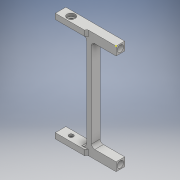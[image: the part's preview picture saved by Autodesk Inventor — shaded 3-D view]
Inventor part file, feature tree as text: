
AUTODESK INVENTOR PART (.ipt)
format: ipt  version: 2018 (Build 220112000, 112)  size: 381,952 bytes
history: native  units: mm
features: sketch x10, extrude x9, fillet x4
ambient origin geometry x8: Origin, YZ Plane, XZ Plane, XY Plane, X Axis, Y Axis, Z Axis, Center Point
bodies: Solid1 (feature_tree)
feature tree (23):
  extrude  "Extrusion1"  Depth=5.5118mm
  extrude  "Extrusion2"  Depth=2.3368mm
  extrude  "Extrusion3"  Depth=5.5118mm
  fillet  "Fillet1"  Radius=5.588mm
  fillet  "Fillet2"  Radius=2.3368mm
  extrude  "Extrusion4"  Depth=5.0mm
  extrude  "Extrusion5"  Depth=10.763mm
  extrude  "Extrusion6"  Depth=30.0mm TaperAngle=0.0deg
  extrude  "Extrusion7"  Depth=5.0mm
  fillet  "Fillet3"  Radius=10.763mm
  sketch  "Sketch8"  dims[d22=8.1mm d23=114.75mm d24=0.0mm]
  extrude  "Extrusion8"  Depth=114.75mm TaperAngle=0.0deg
  extrude  "Extrusion9"  Depth=2.412mm TaperAngle=0.0deg
  fillet  "Fillet4"  Radius=4.5mm
  sketch  "Sketch1"  dims[d0=8.763mm d1=5.5118mm]
  sketch  "Sketch2"  dims[d4=5.588mm d5=2.3368mm]
  sketch  "Sketch3"  dims[d6=8.763mm d7=5.5118mm d8=5.588mm d9=2.3368mm]
  sketch  "Sketch4"  dims[d10=30.0mm d11=0.0mm d12=5.0mm]
  sketch  "Sketch5"  dims[d13=111.0mm d14=0.0mm d15=10.763mm]
  sketch  "Sketch6"  dims[d16=10.763mm d17=30.0mm d18=0.0mm]
  sketch  "Sketch7"  dims[d19=2.0mm d20=5.0mm d21=10.763mm]
  sketch  "Sketch9"  dims[d25=2.412mm d26=0.0mm d27=2.412mm d28=0.0mm d29=4.5mm]
  sketch  "Sketch10"  dims[d30=115.0mm d31=0.0mm d32=0.5mm d33=8.763mm d34=8.763mm d35=29.5mm d36=0.0mm d37=6.5mm d38=6.5mm d39=24.75mm d40=0.0mm d41=3.25mm]
